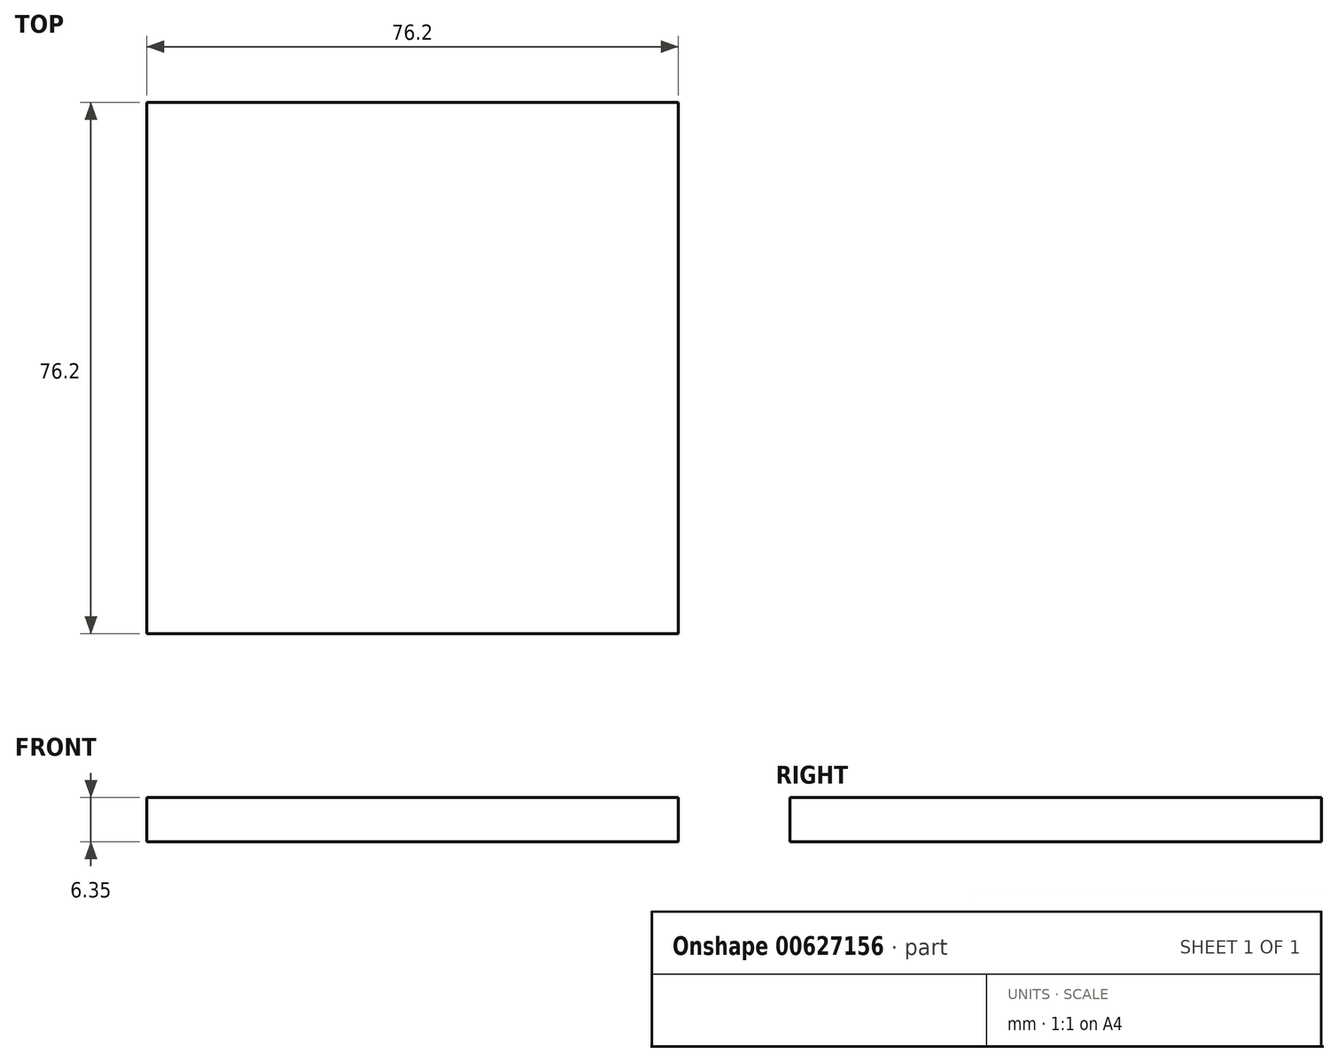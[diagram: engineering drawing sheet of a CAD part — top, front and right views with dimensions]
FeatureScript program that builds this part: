
annotation { "Feature Type Name" : "Feature", "Feature Type Description" : "" }
export const myFeature = defineFeature(function(context is Context, id is Id, definition is map)
    precondition{}
    {
        {
            var Q0;
            Q0=qCreatedBy(makeId("Top.planeOp"),FACE);
            var sketch = newSketch(context, id + "F0", { "sketchPlane" : qUnion([Q0])});
            skLineSegment(sketch, "E0.bottom", {"start": v(-76.2, 0) * mm, "end": v(0, 0) * mm});
            skLineSegment(sketch, "E0.top", {"start": v(-76.2, 76.2) * mm, "end": v(0, 76.2) * mm});
            skLineSegment(sketch, "E0.left", {"start": v(-76.2, 0) * mm, "end": v(-76.2, 76.2) * mm});
            skLineSegment(sketch, "E0.right", {"start": v(0, 0) * mm, "end": v(0, 76.2) * mm});
            skSolve(sketch);
        }
        {
            var Q0;
            Q0 = qSketchRegion(id + "F0", true);
            extrude(context, id + "F1", {"entities" : qUnion([Q0]), "depth" : 6.35 * mm, "offsetDistance" : 25 * mm});
        }
    });
